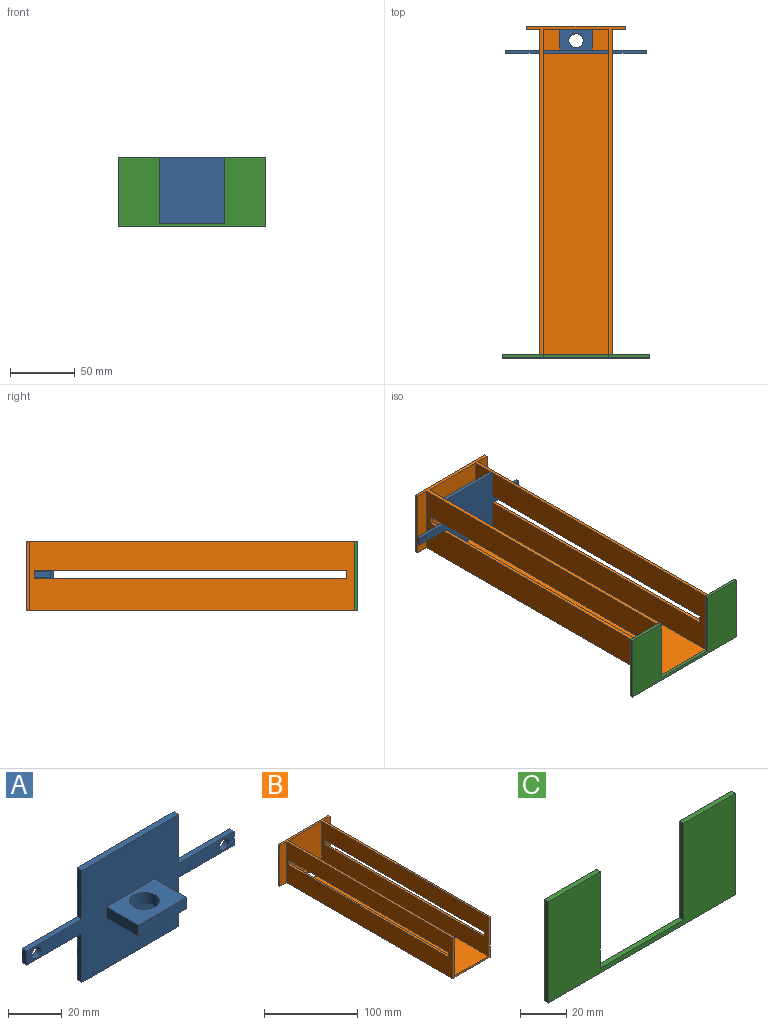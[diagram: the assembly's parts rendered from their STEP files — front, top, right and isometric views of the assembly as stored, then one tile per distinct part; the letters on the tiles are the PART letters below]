
ASSEMBLY  parts=3 mates=5
PART A: 22 faces, bbox 108.6x19.4x50.8 mm
  f0: plane 22.23x2.54mm, normal (1,0,0), area 56.5mm2, adj f1,f12,f14,f15
  f1: plane 28.91x2.54mm, normal (0,0,-1), area 73.4mm2, adj f0,f2,f14,f15
  f2: plane 6.35x2.54mm, normal (1,0,0), area 16.1mm2, adj f1,f3,f14,f15
  f3: plane 28.91x2.54mm, normal (0,0,1), area 73.4mm2, adj f2,f4,f14,f15
  f4: plane 22.23x2.54mm, normal (1,0,0), area 56.5mm2, adj f3,f5,f14,f15
  f5: plane 50.8x2.54mm, normal (0,0,1), area 129mm2, adj f4,f6,f14,f15
  f6: plane 22.23x2.54mm, normal (-1,0,0), area 56.5mm2, adj f5,f7,f14,f15
  f7: plane 28.91x2.54mm, normal (0,0,1), area 73.4mm2, adj f6,f8,f14,f15
  f8: plane 6.35x2.54mm, normal (-1,0,0), area 16.1mm2, adj f7,f9,f14,f15
  f9: plane 28.91x2.54mm, normal (0,0,-1), area 73.4mm2, adj f8,f10,f14,f15
  f10: plane 22.23x2.54mm, normal (-1,0,0), area 56.5mm2, adj f9,f12,f14,f15
  f11: cylinder r=2.54mm len=5.08mm, axis (0,1,0), area 40.5mm2, adj f14,f15
  f12: plane 50.8x2.54mm, normal (0,0,-1), area 129mm2, adj f0,f10,f14,f15
  f13: cylinder r=2.54mm len=5.08mm, axis (0,1,0), area 40.5mm2, adj f14,f15
  f14: plane 108.61x50.8mm, normal (0,-1,0), area 2778.2mm2, adj f0,f1,f2,f3,f4,f5,f6,f7
  f15: plane 108.61x50.8mm, normal (0,1,0), area 2907.2mm2, adj f0,f1,f2,f3,f4,f5,f6,f7
  f16: plane 16.89x5.08mm, normal (-1,0,0), area 85.8mm2, adj f14,f17,f20,f21
  f17: plane 25.4x5.08mm, normal (0,-1,0), area 129mm2, adj f16,f19,f20,f21
  f18: cylinder r=5.55mm len=11.11mm, axis (0,0,-1), area 177.3mm2, adj f20,f21
  f19: plane 16.89x5.08mm, normal (1,0,0), area 85.8mm2, adj f14,f17,f20,f21
  f20: plane 25.4x16.89mm, normal (0,0,1), area 332.2mm2, adj f14,f16,f17,f18,f19
  f21: plane 25.4x16.89mm, normal (0,0,-1), area 332.2mm2, adj f14,f16,f17,f18,f19
PART B: 23 faces, bbox 76.2x254x53.3 mm
  f0: plane 251.46x50.8mm, normal (1,0,0), area 11241.9mm2, adj f4,f6,f7,f13,f14,f15,f16,f17
  f1: plane 251.46x53.34mm, normal (-1,0,0), area 11880.6mm2, adj f2,f4,f7,f13,f14,f15,f16,f20
  f2: plane 254x76.2mm, normal (0,0,-1), area 14102.7mm2, adj f1,f3,f7,f8,f18,f19,f20,f21
  f3: plane 251.46x53.34mm, normal (1,0,0), area 11880.6mm2, adj f2,f4,f7,f9,f10,f11,f12,f19
  f4: plane 254x76.2mm, normal (0,0,1), area 1471mm2, adj f0,f1,f3,f5,f7,f8,f17,f18
  f5: plane 251.46x50.8mm, normal (-1,0,0), area 11241.9mm2, adj f4,f6,f7,f9,f10,f11,f12,f17
  f6: plane 251.46x50.8mm, normal (0,0,1), area 12631.7mm2, adj f0,f5,f7,f17,f22
  f7: plane 55.88x53.34mm, normal (0,-1,0), area 400mm2, adj f0,f1,f2,f3,f4,f5,f6
  f8: plane 76.2x53.34mm, normal (0,1,0), area 4064.5mm2, adj f2,f4,f18,f21
  f9: plane 241.3x2.54mm, normal (0,0,-1), area 612.9mm2, adj f3,f5,f10,f12
  f10: plane 6.35x2.54mm, normal (0,1,0), area 16.1mm2, adj f3,f5,f9,f11
  f11: plane 241.3x2.54mm, normal (0,0,1), area 612.9mm2, adj f3,f5,f10,f12
  f12: plane 6.35x2.54mm, normal (0,-1,0), area 16.1mm2, adj f3,f5,f9,f11
  f13: plane 6.35x2.54mm, normal (0,-1,0), area 16.1mm2, adj f0,f1,f14,f16
  f14: plane 241.3x2.54mm, normal (0,0,1), area 612.9mm2, adj f0,f1,f13,f15
  f15: plane 6.35x2.54mm, normal (0,1,0), area 16.1mm2, adj f0,f1,f14,f16
  f16: plane 241.3x2.54mm, normal (0,0,-1), area 612.9mm2, adj f0,f1,f13,f15
  f17: plane 50.8x50.8mm, normal (0,-1,0), area 2580.6mm2, adj f0,f4,f5,f6
  f18: plane 53.34x2.54mm, normal (1,0,0), area 135.5mm2, adj f2,f4,f8,f19
  f19: plane 53.34x10.16mm, normal (0,-1,0), area 541.9mm2, adj f2,f3,f4,f18
  f20: plane 53.34x10.16mm, normal (0,-1,0), area 541.9mm2, adj f1,f2,f4,f21
  f21: plane 53.34x2.54mm, normal (-1,0,0), area 135.5mm2, adj f2,f4,f8,f20
  f22: cylinder r=6.73mm len=13.47mm, axis (0,0,-1), area 107.5mm2, adj f2,f6
PART C: 10 faces, bbox 114.3x2.5x53.3 mm
  f0: plane 31.75x2.54mm, normal (0,0,1), area 80.6mm2, adj f1,f7,f8,f9
  f1: plane 50.8x2.54mm, normal (-1,0,0), area 129mm2, adj f0,f2,f8,f9
  f2: plane 50.8x2.54mm, normal (0,0,1), area 129mm2, adj f1,f3,f8,f9
  f3: plane 50.8x2.54mm, normal (1,0,0), area 129mm2, adj f2,f4,f8,f9
  f4: plane 31.75x2.54mm, normal (0,0,1), area 80.6mm2, adj f3,f5,f8,f9
  f5: plane 53.34x2.54mm, normal (-1,0,0), area 135.5mm2, adj f4,f6,f8,f9
  f6: plane 114.3x2.54mm, normal (0,0,-1), area 290.3mm2, adj f5,f7,f8,f9
  f7: plane 53.34x2.54mm, normal (1,0,0), area 135.5mm2, adj f0,f6,f8,f9
  f8: plane 114.3x53.34mm, normal (0,1,0), area 3516.1mm2, adj f0,f1,f2,f3,f4,f5,f6,f7
  f9: plane 114.3x53.34mm, normal (0,-1,0), area 3516.1mm2, adj f0,f1,f2,f3,f4,f5,f6,f7
PLACE A rot(axis=(0,0,1),180deg) t=(42.55,34.1,-2.59)mm
PLACE B t=(42.55,55.2,-30.53)mm
PLACE C t=(42.55,52.66,-30.53)mm fixed
MATE planar C.f3 <-> B.f0  axis (1,0,0) through (17.15,-200.07,-2.59)mm
MATE planar A.f7 <-> B.f9  axis (0,0,1) through (82.41,35.37,0.58)mm
MATE planar B.f7 <-> C.f8  axis (0,-1,0) through (42.55,-198.8,-12.06)mm
MATE planar B.f5 <-> A.f6  axis (-1,0,0) through (67.95,-73.25,-2.59)mm
MATE planar B.f6 <-> C.f2  axis (0,0,1) through (42.55,-198.8,-27.99)mm
